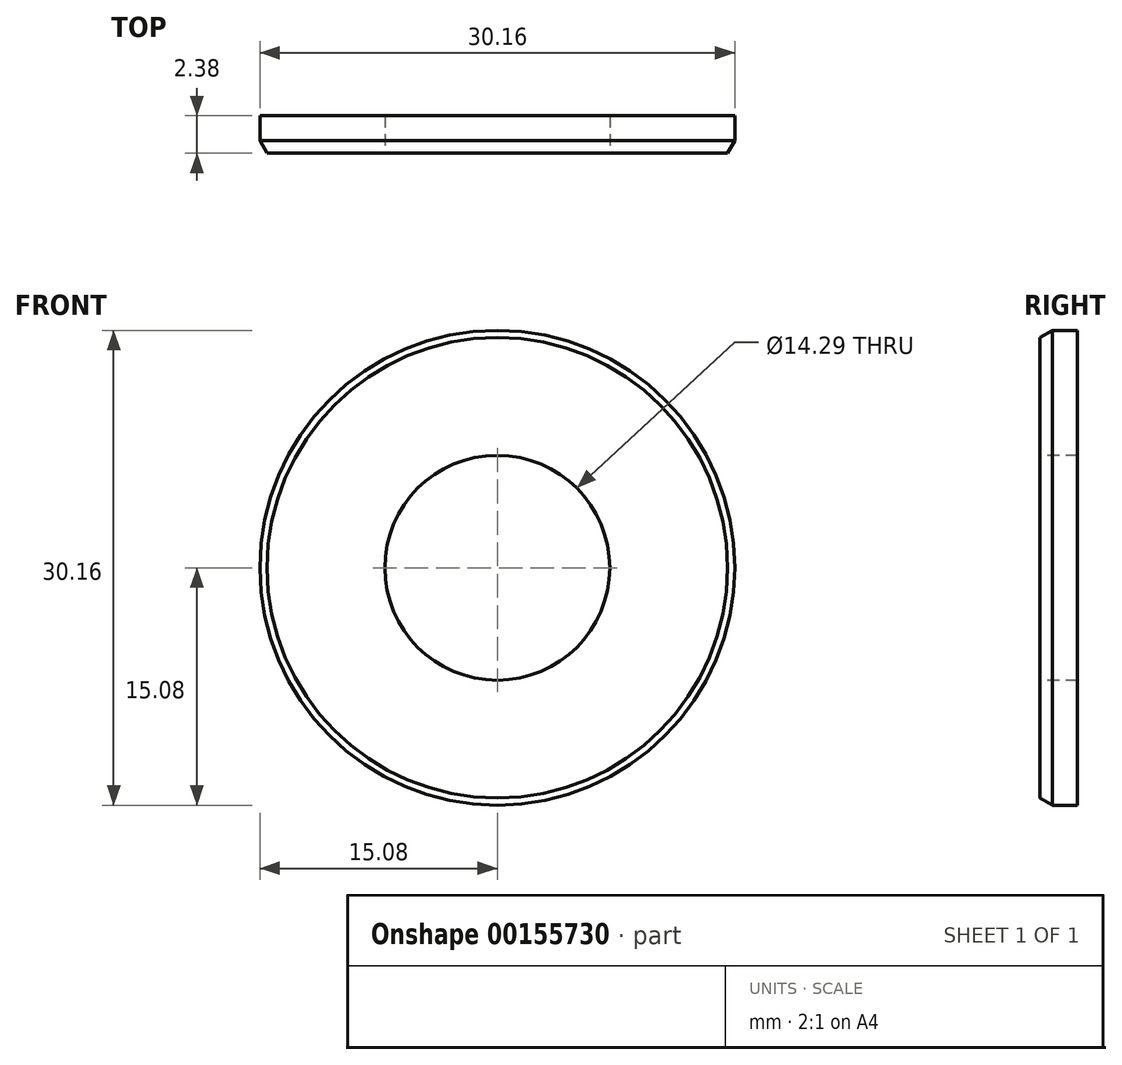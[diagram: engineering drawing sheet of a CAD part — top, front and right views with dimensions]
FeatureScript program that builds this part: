
annotation { "Feature Type Name" : "Feature", "Feature Type Description" : "" }
export const myFeature = defineFeature(function(context is Context, id is Id, definition is map)
    precondition{}
    {
        {
            var Q0;
            Q0=qCreatedBy(makeId("Right.planeOp"),FACE);
            var sketch = newSketch(context, id + "F0", { "sketchPlane" : qUnion([Q0])});
            skLineSegment(sketch, "E0", {"start": v(-1.2, 14.62) * mm, "end": v(-1.2, 7.14) * mm});
            skLineSegment(sketch, "E1", {"start": v(-1.2, 7.14) * mm, "end": v(1.2, 7.14) * mm});
            skLineSegment(sketch, "E2", {"start": v(1.2, 7.14) * mm, "end": v(1.2, 15.08) * mm});
            skLineSegment(sketch, "E3", {"start": v(1.2, 15.08) * mm, "end": v(-0.4, 15.08) * mm});
            skLineSegment(sketch, "E4", {"start": v(-0.4, 15.08) * mm, "end": v(-1.2, 14.62) * mm});
            skLineSegment(sketch, "E5", {"start": v(-7.32, 0) * mm, "end": v(7.71, 0) * mm, "construction": true});
            skSolve(sketch);
        }
        {
            var Q0;
            Q0=qSketchRegion(id+"F0",true);
            var Q1;
            Q1=sQuery(id+"F0.wireOp",EDGE,"E5");
            revolve(context, id + "F1", {"entities" : qUnion([Q0]), "axis" : qUnion([Q1]), "revolveType" : RevolveType.FULL});
        }
    });
